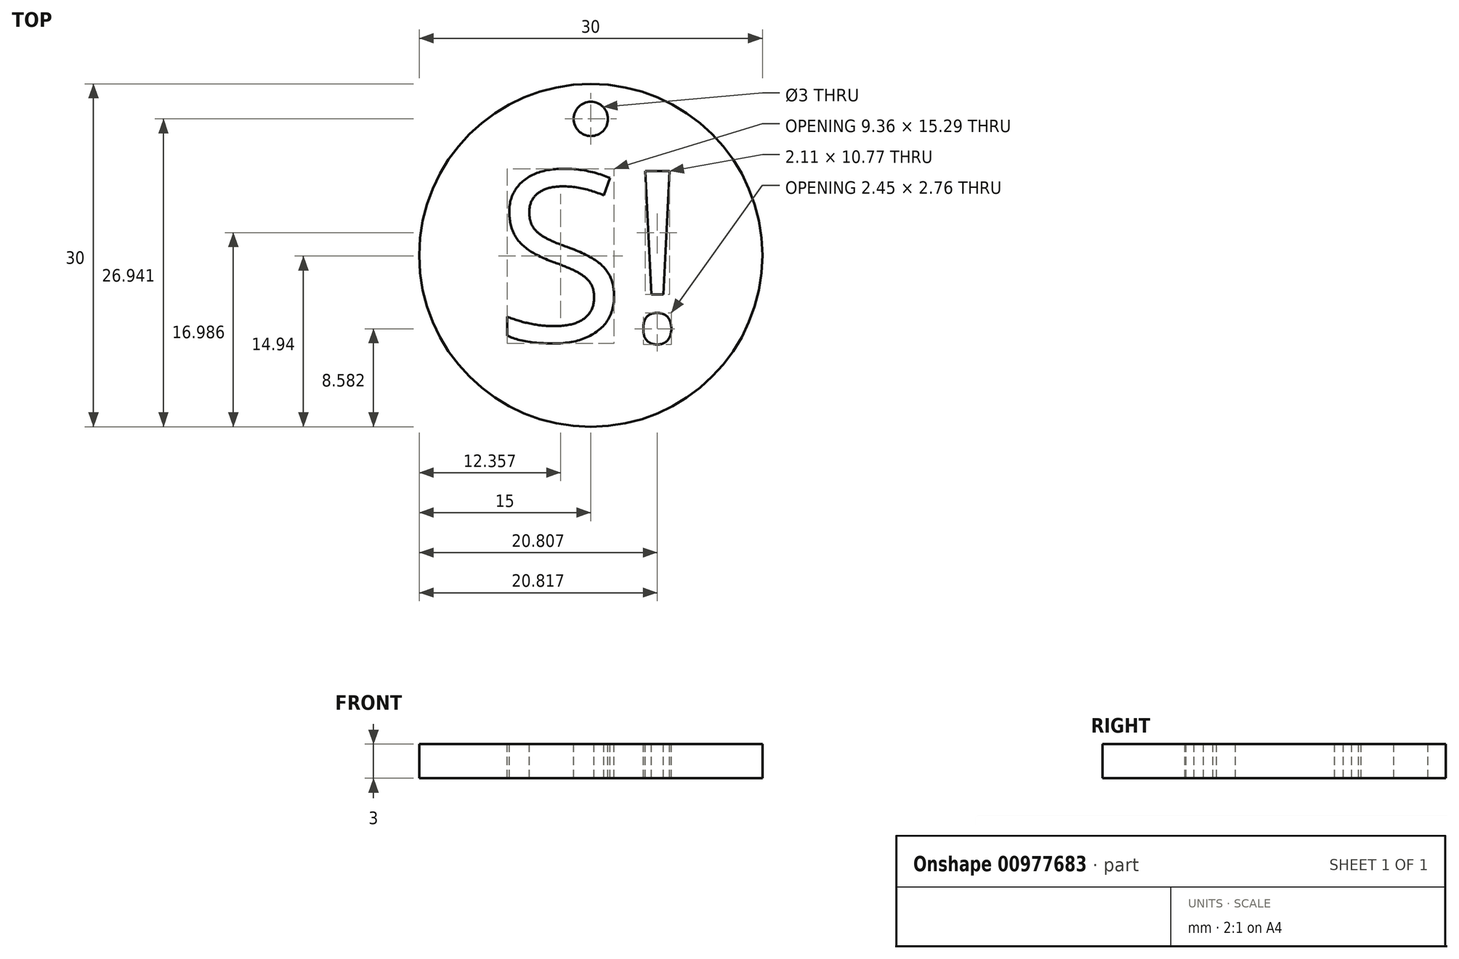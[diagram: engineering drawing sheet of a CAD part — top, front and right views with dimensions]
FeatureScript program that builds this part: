
annotation { "Feature Type Name" : "Feature", "Feature Type Description" : "" }
export const myFeature = defineFeature(function(context is Context, id is Id, definition is map)
    precondition{}
    {
        {
            var Q0;
            Q0=qCreatedBy(makeId("Top.planeOp"),FACE);
            var sketch = newSketch(context, id + "F0", { "sketchPlane" : qUnion([Q0])});
            skCircle(sketch, "E0", {"center": v(0, 0) * mm, "radius": 15 * mm});
            skSolve(sketch);
        }
        {
            var Q0;
            Q0 = qSketchRegion(id + "F0", true);
            extrude(context, id + "F1", {"entities" : qUnion([Q0]), "depth" : 3 * mm, "offsetDistance" : 25 * mm});
        }
        {
            var Q0;
            Q0=makeQuery(id+"F1.opExtrude","CAP_FACE",FACE,{"disambiguationData":[OSD([sQuery(id+"F0.wireOp",EDGE,"E0")])],"isStart":false});
            var sketch = newSketch(context, id + "F2", { "sketchPlane" : qUnion([Q0])});
            skText(sketch, "E1", { "text": "S!", "fontName": "OpenSans-Regular.ttf"});
            skCircle(sketch, "E2", {"center": v(0, 11.94) * mm, "radius": 1.5 * mm});
            const initialGuessF2  = {"E1": [-0.0084, -0.0075, 1, 0, 0.015]};
            skSetInitialGuess(sketch, initialGuessF2);
            skSolve(sketch);
        }
        {
            var Q0;
            Q0 = qSketchRegion(id + "F2", true);
            extrude(context, id + "F3", {"entities" : qUnion([Q0]), "operationType" : NewBodyOperationType.REMOVE, "endBound" : BoundingType.THROUGH_ALL, "oppositeDirection" : true, "depth" : 25 * mm, "offsetDistance" : 25 * mm});
        }
    });
